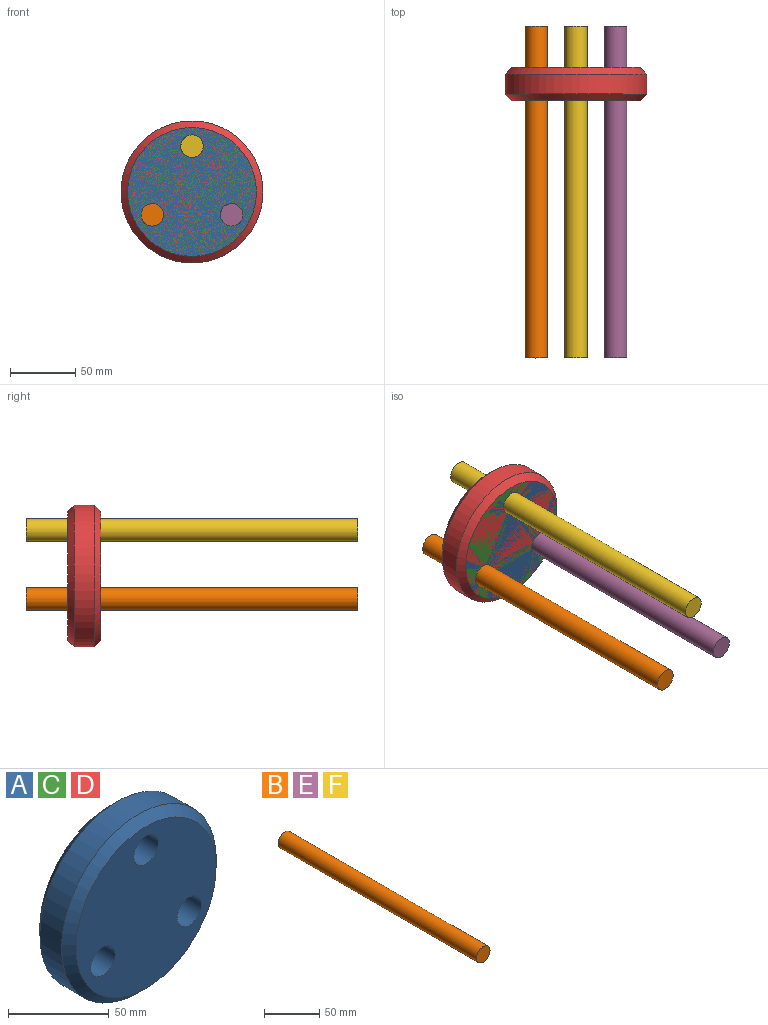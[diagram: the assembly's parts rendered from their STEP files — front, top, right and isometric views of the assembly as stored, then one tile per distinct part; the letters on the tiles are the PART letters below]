
ASSEMBLY  parts=6 mates=1
PART A: 8 faces, bbox 108.7x25.4x108.7 mm
  f0: cylinder r=8.56mm len=25.4mm, axis (0,1,0), area 1366.3mm2, adj f4,f5
  f1: cylinder r=8.56mm len=25.4mm, axis (0,1,0), area 1366.3mm2, adj f4,f5
  f2: cylinder r=8.56mm len=25.4mm, axis (0,1,0), area 1366.3mm2, adj f4,f5
  f3: cylinder r=54.37mm len=108.74mm, axis (0,1,0), area 5206.3mm2, adj f6,f7
  f4: plane 98.58x98.58mm, normal (0,-1,0), area 6941.9mm2, adj f0,f1,f2,f7
  f5: plane 98.58x98.58mm, normal (0,1,0), area 6941.9mm2, adj f0,f1,f2,f6
  f6: cone r=54.37mm half-angle=45deg, axis (0,-1,0), area 2339.6mm2, adj f3,f5
  f7: cone r=49.29mm half-angle=45deg, axis (0,1,0), area 2339.6mm2, adj f3,f4
PART B: 3 faces, bbox 17.1x254x17.1 mm
  f0: cylinder r=8.56mm len=254mm, axis (0,1,0), area 13662.8mm2, adj f1,f2
  f1: plane 17.12x17.12mm, normal (0,-1,0), area 230.3mm2, adj f0
  f2: plane 17.12x17.12mm, normal (0,1,0), area 230.3mm2, adj f0
PART C: same geometry as A
PART D: same geometry as A
PART E: same geometry as B
PART F: same geometry as B
PLACE A rot(axis=(0,-1,0),0deg) t=(-123.74,59.36,-72.71)mm
PLACE B rot(axis=(0,1,0),108deg) t=(-146.79,91.08,-124.53)mm
PLACE C rot(axis=(0,-1,0),120deg) t=(-123.74,59.36,-72.71)mm fixed
PLACE D rot(axis=(0,1,0),120deg) t=(-123.74,59.36,-72.71)mm
PLACE E rot(axis=(0,-1,0),12deg) t=(-67.33,91.08,-66.77)mm
PLACE F rot(axis=(0,-1,0),132deg) t=(-157.09,91.08,-26.84)mm
MATE cylindrical B.f0 <-> A.f1  axis (0,1,0) through (-154.1,-35.92,-90.24)mm
